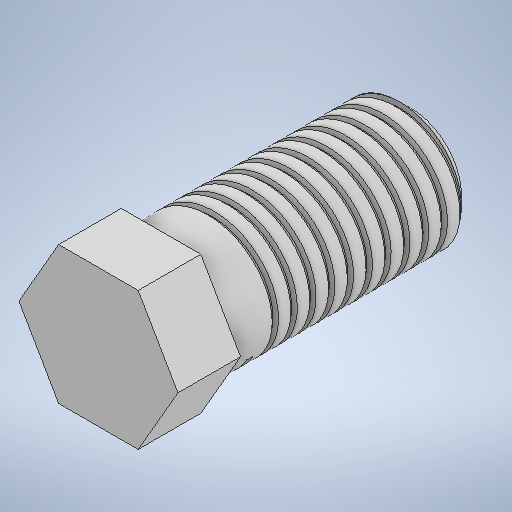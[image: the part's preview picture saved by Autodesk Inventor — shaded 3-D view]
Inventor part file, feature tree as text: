
AUTODESK INVENTOR PART (.ipt)
format: ipt  version: 2025.2 (Build 292293000, 293)  size: 479,744 bytes
history: native  units: mm
features: sketch x3, other x2, extrude x2, chamfer x1
ambient origin geometry x8: Origin, YZ Plane, XZ Plane, XY Plane, X Axis, Y Axis, Z Axis, Center Point
bodies: Body1 (feature_tree)
feature tree (8):
  other  "Sólido1"
  extrude  "Extrusão1"  Depth=20.0mm TaperAngle=0.0deg
  other  "Espiral1"
  chamfer  "Chanfro1"  Distance=11.0mm
  extrude  "Extrusão2"  Depth=10.0mm TaperAngle=0.0deg
  sketch  "Esboço1"  dims[d0=20.0mm d1=40.0mm d2=0.0mm]
  sketch  "Esboço2"  dims[d6=1.0mm]
  sketch  "Esboço5"  dims[d7=0.2mm d8=3.0mm d9=35.0mm d10=10.0mm d11=0.0mm d12=90.0deg d13=90.0deg d14=0.0mm d15=0.0mm d16=2.0mm d17=2.0mm d18=45.0deg d20=11.0mm d21=10.0mm d22=0.0mm d24=0.5mm d25=0.872665mm d26=0.5mm d27=0.872665mm]
